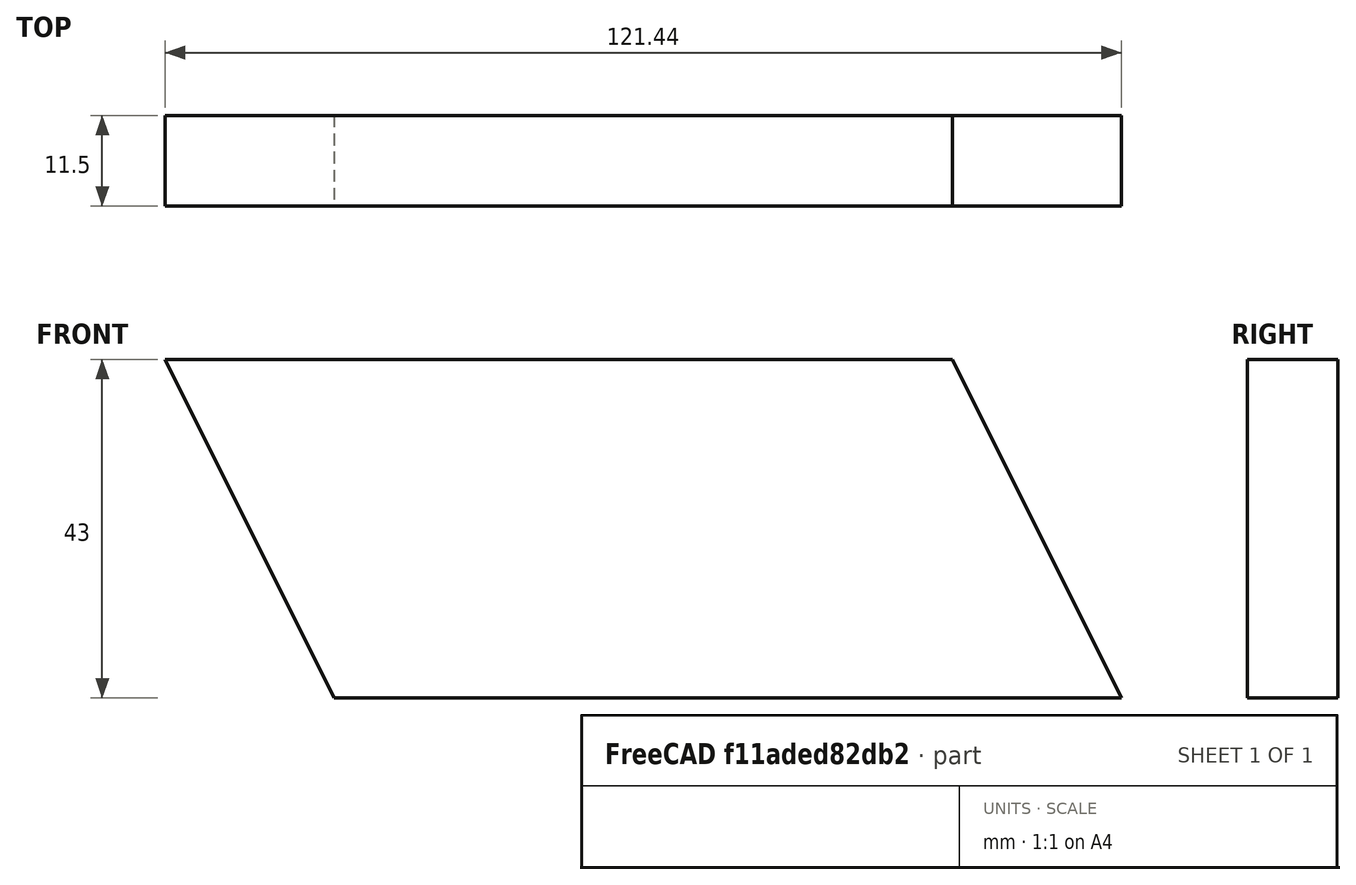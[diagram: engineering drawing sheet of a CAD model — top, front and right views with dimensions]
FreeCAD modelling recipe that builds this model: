
FCSTD DOCUMENT
Label: X_SY_M
objects: Sketcher::SketchObject×1, PartDesign::Pad×1
note: 3 computed .brp shape members not serialized (recipe doc carries the construction recipe); baked Part::Feature solids carry a one-line shape summary decoded from their .brp

FEATURE [Sketcher::SketchObject] Sketch
  Placement = pos=(0,0,0) rot=(-1,0,0;4.71239rad)
  sketch-geometry (4):
    g0: LineSegment StartX=0 StartY=0 StartZ=0 EndX=100 EndY=0 EndZ=0
    g1: LineSegment StartX=100 StartY=0 StartZ=0 EndX=78.561 EndY=43 EndZ=0
    g2: LineSegment StartX=78.561 StartY=43 StartZ=0 EndX=-21.439 EndY=43 EndZ=0
    g3: LineSegment StartX=-21.439 StartY=43 StartZ=0 EndX=0 EndY=0 EndZ=0
  constraints (11):
    c: Horizontal(g0)
    c: Coincident(g0,g1)
    c: Coincident(g1,g2)
    c: Horizontal(g2)
    c: Coincident(g2,g3)
    c: Coincident(g3,g-1)
    c: Equal(g0,g2)
    c: DistanceX(g2) = -100
    c: Angle(g3,g2) = 1.10828
    c: DistanceY(g3) = -43
    c: Coincident(g-1,g0)
FEATURE [PartDesign::Pad] Pad
  Length = 11.5
  Length2 = 100
  Placement = pos=(0,0,0) rot=(-1,0,0;4.71239rad)
  Sketch = -> Sketch
  Type = 0
